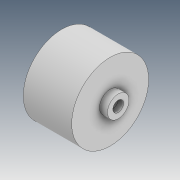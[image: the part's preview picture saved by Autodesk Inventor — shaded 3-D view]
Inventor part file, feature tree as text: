
AUTODESK INVENTOR PART (.ipt)
format: ipt  version: 2021 (Build 250183000, 183)  size: 116,736 bytes
history: native  units: in
note: dims shown in document units (in); Inventor stores cm internally (conversion verified against a paired STEP export)
features: sketch x6, extrude x3, other x2
ambient origin geometry x8: Origin, YZ Plane, XZ Plane, XY Plane, X Axis, Y Axis, Z Axis, Center Point
bodies: Body1 (feature_tree)
feature tree (11):
  other  "Sólido1"
  other  "Revolução1"
  extrude  "Extrusão1"  Depth=0.2815in
  extrude  "Extrusão2"  Depth=0.0984in
  sketch  "Esboço4"  dims[d6=0.0591in d7=0.0in]
  sketch  "Esboço5"  dims[d8=0.1181in]
  extrude  "Extrusão3"  Depth=0.1575in
  sketch  "Esboço1"  dims[d0=0.3543in d1=0.2815in]
  sketch  "Esboço2"  dims[d2=0.0787in d3=0.0984in]
  sketch  "Esboço3"  dims[d4=90.0deg d5=0.1575in]
  sketch  "Esboço6"  dims[d9=0.1575in d10=0.0in d11=0.0787in d12=0.0417in d13=0.0in]
